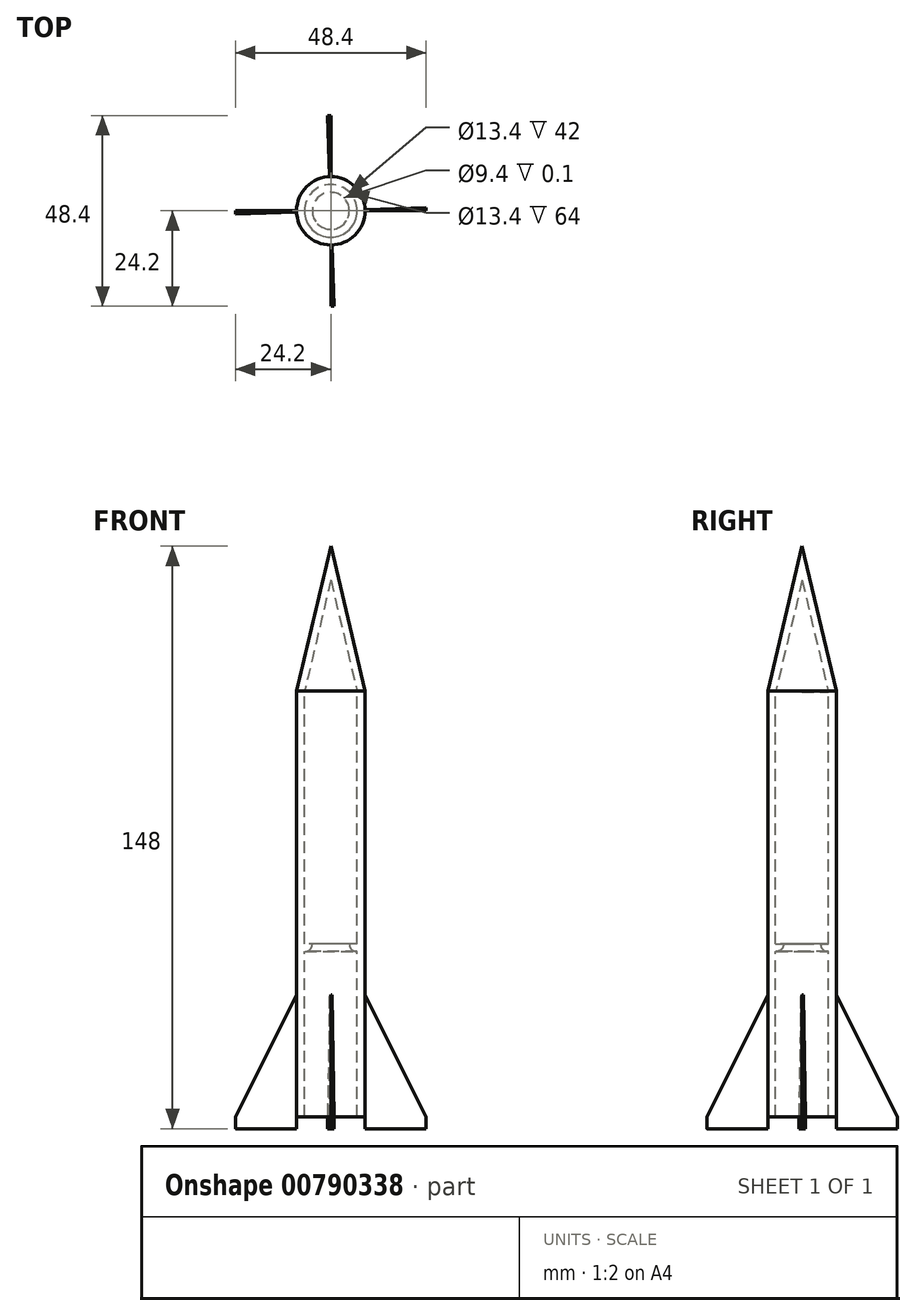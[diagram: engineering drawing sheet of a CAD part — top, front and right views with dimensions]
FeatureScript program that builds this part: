
annotation { "Feature Type Name" : "Feature", "Feature Type Description" : "" }
export const myFeature = defineFeature(function(context is Context, id is Id, definition is map)
    precondition{}
    {
        {
            var Q0;
            Q0=qCreatedBy(makeId("Front.planeOp"),FACE);
            var sketch = newSketch(context, id + "F0", { "sketchPlane" : qUnion([Q0])});
            skLineSegment(sketch, "E0", {"start": v(0, 145) * mm, "end": v(0, 143) * mm});
            skLineSegment(sketch, "E1", {"start": v(0, 143) * mm, "end": v(-13.5, 143) * mm});
            skLineSegment(sketch, "E2", {"start": v(-6.7, 108) * mm, "end": v(-6.7, 0) * mm});
            skLineSegment(sketch, "E3.1", {"start": v(-8.7, 108.2) * mm, "end": v(-8.7, 0) * mm});
            skLineSegment(sketch, "E4", {"start": v(-8.7, 0) * mm, "end": v(-6.7, 0) * mm});
            skLineSegment(sketch, "E5", {"start": v(-6.7, 0) * mm, "end": v(-6.7, 42) * mm});
            skLineSegment(sketch, "E6", {"start": v(-6.7, 42) * mm, "end": v(-4.7, 42) * mm});
            skLineSegment(sketch, "E7", {"start": v(-4.7, 42) * mm, "end": v(-4.7, 44) * mm});
            skLineSegment(sketch, "E8", {"start": v(-4.7, 44) * mm, "end": v(-6.7, 44) * mm});
            skLineSegment(sketch, "E9", {"start": v(0, 145) * mm, "end": v(0, 0) * mm});
            skLineSegment(sketch, "E10", {"start": v(0, 145) * mm, "end": v(-8.7, 108.2) * mm});
            skLineSegment(sketch, "E11", {"start": v(-6.7, 108) * mm, "end": v(0, 108) * mm, "construction": true});
            skLineSegment(sketch, "E12", {"start": v(-8.7, 108.2) * mm, "end": v(0, 108) * mm, "construction": true});
            skLineSegment(sketch, "E13", {"start": v(-6.7, 108) * mm, "end": v(0, 136.34) * mm});
            skSolve(sketch);
        }
        {
            var Q0;
            {var subQ0=sQuery(id+"F0.wireOp",EDGE,"E3.1");Q0=makeQuery(id+"F0.imprint","IMPRINT",FACE,{"disambiguationData":[TD([[makeQuery(id+"F0.imprint","IMPRINT",EDGE,{"derivedFrom":subQ0}),1.0]])]});}
            var Q1;
            {var subQ0=sQuery(id+"F0.wireOp",EDGE,"E6");Q1=makeQuery(id+"F0.imprint","IMPRINT",FACE,{"disambiguationData":[TD([[makeQuery(id+"F0.imprint","IMPRINT",EDGE,{"derivedFrom":subQ0}),1.0]])]});}
            var Q2;
            {var subQ0=sQuery(id+"F0.wireOp",EDGE,"E9");var subQ1=sQuery(id+"F0.wireOp",EDGE,"E1");var subQ2=makeQuery(id+"F0.imprint","INTERSECT",VERTEX,{"derivedFrom":[subQ1,subQ0]});Q2=makeQuery(id+"F0.imprint","IMPRINT",FACE,{"disambiguationData":[TD([[makeQuery(id+"F0.imprint","IMPRINT",EDGE,{"disambiguationData":[TD([[subQ2,-1.0]])],"derivedFrom":subQ1}),-1.0]])]});}
            var Q3;
            Q3=sQuery(id+"F0.wireOp",EDGE,"E9");
            revolve(context, id + "F1", {"surfaceOperationType" : NewSurfaceOperationType.NEW, "entities" : qUnion([Q0, Q1, Q2]), "axis" : qUnion([Q3]), "revolveType" : RevolveType.FULL});
        }
        {
            var Q0;
            Q0=qCreatedBy(makeId("Right.planeOp"),FACE);
            var sketch = newSketch(context, id + "F2", { "sketchPlane" : qUnion([Q0])});
            skLineSegment(sketch, "E14", {"start": v(8.7, -3) * mm, "end": v(24.2, -3) * mm});
            skLineSegment(sketch, "E15", {"start": v(24.2, -3) * mm, "end": v(24.2, 0) * mm});
            skLineSegment(sketch, "E16", {"start": v(8.7, 0) * mm, "end": v(8.7, 31) * mm});
            skLineSegment(sketch, "E17", {"start": v(8.7, 31) * mm, "end": v(24.2, 0) * mm});
            skLineSegment(sketch, "E18", {"start": v(8.7, -3) * mm, "end": v(8.7, 0) * mm});
            skLineSegment(sketch, "E19", {"start": v(0, 0) * mm, "end": v(0, 51.2) * mm});
            skLineSegment(sketch, "E20", {"start": v(8.7, 0) * mm, "end": v(0, 0) * mm, "construction": true});
            skSolve(sketch);
        }
        {
            var Q0;
            Q0=makeQuery(id+"F2.imprint","IMPRINT",FACE,{"disambiguationData":[TD([[makeQuery(id+"F2.imprint","IMPRINT",EDGE,{"derivedFrom":sQuery(id+"F2.wireOp",EDGE,"E14")}),1.0]])]});
            var Q1;
            Q1=sQuery(id+"F2.wireOp",EDGE,"E19");
            revolve(context, id + "F3", {"surfaceOperationType" : NewSurfaceOperationType.NEW, "entities" : qUnion([Q0]), "axis" : qUnion([Q1]), "revolveType" : RevolveType.ONE_DIRECTION, "angle" : 2 * degree});
        }
        {
            var Q0;
            Q0=makeQuery(id+"F3.opRevolve","SWEPT_BODY",BODY,{"disambiguationData":[OSD([sQuery(id+"F2.wireOp",EDGE,"E14"),sQuery(id+"F2.wireOp",EDGE,"E15"),sQuery(id+"F2.wireOp",EDGE,"E16"),sQuery(id+"F2.wireOp",EDGE,"E17"),sQuery(id+"F2.wireOp",EDGE,"E18")])]});
            var Q1;
            Q1=sQuery(id+"F2.wireOp",EDGE,"E19");
            circularPattern(context, id + "F4", {"entities" : qUnion([Q0]), "axis" : qUnion([Q1]), "angle" : 360 * degree, "instanceCount" : 4, "equalSpace" : true});
        }
        {
            var Q0;
            Q0=makeQuery(id+"F1.opRevolve","SWEPT_EDGE",EDGE,{"disambiguationData":[OSD([sQuery(id+"F0.wireOp",EDGE,"E6"),sQuery(id+"F0.wireOp",EDGE,"E7")])]});
            fillet(context, id + "F5", {"entities" : qUnion([Q0]), "radius" : 1.9 * mm, "tangentPropagation" : true, "allowEdgeOverflow" : false});
        }
    });
